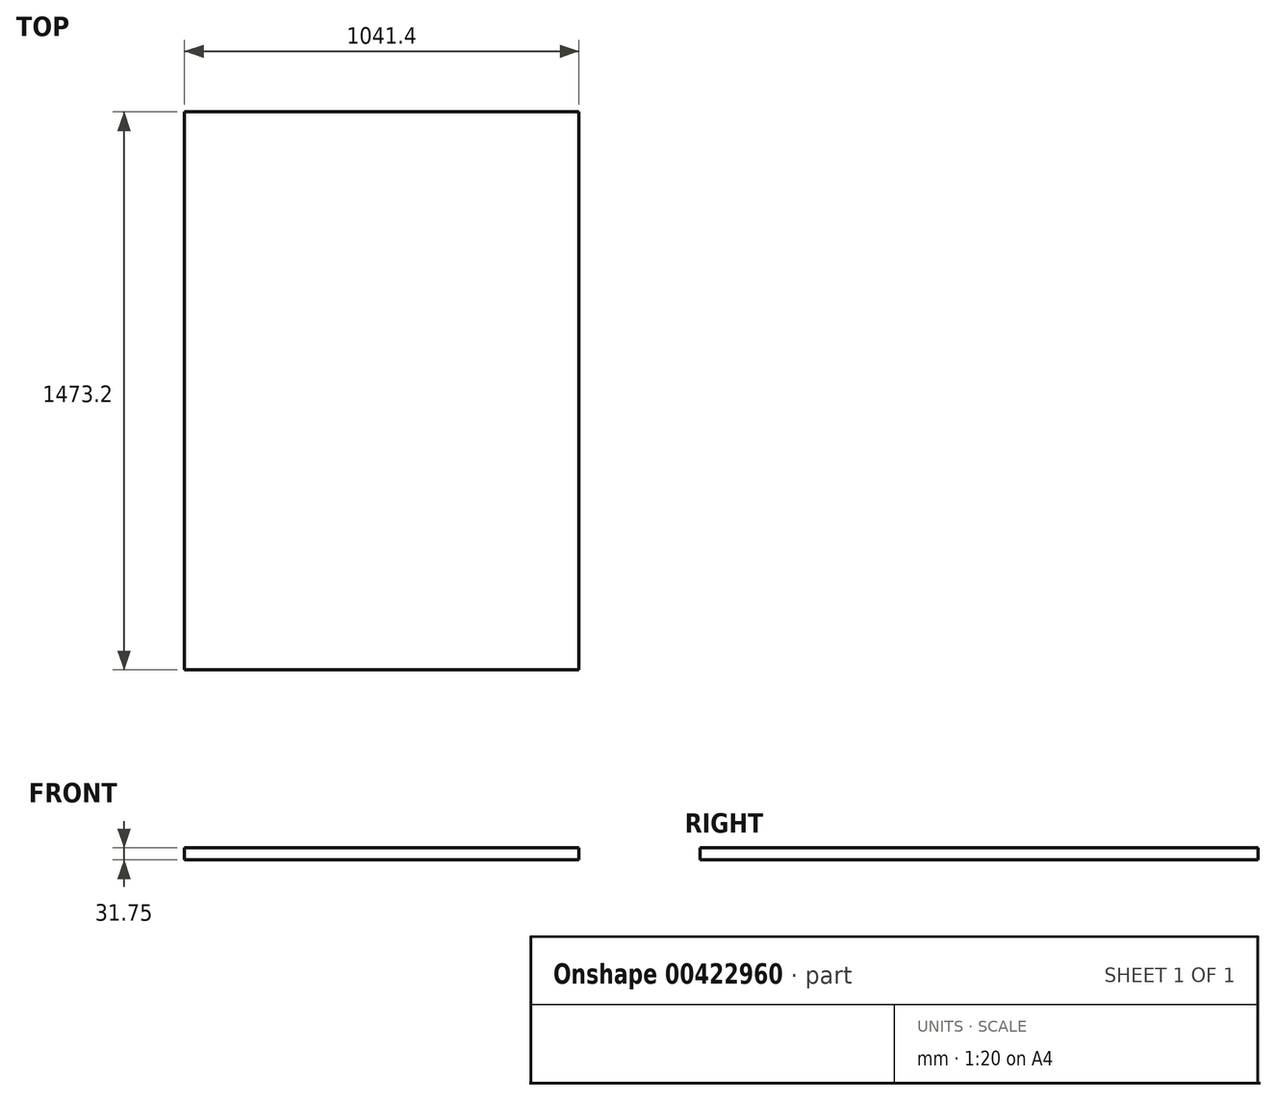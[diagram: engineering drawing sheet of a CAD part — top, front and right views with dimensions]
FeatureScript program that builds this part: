
annotation { "Feature Type Name" : "Feature", "Feature Type Description" : "" }
export const myFeature = defineFeature(function(context is Context, id is Id, definition is map)
    precondition{}
    {
        {
            var Q0;
            Q0=qCreatedBy(makeId("Top.planeOp"),FACE);
            var sketch = newSketch(context, id + "F0", { "sketchPlane" : qUnion([Q0])});
            skLineSegment(sketch, "E0.bottom", {"start": v(520.7, 736.6) * mm, "end": v(-520.7, 736.6) * mm});
            skLineSegment(sketch, "E0.top", {"start": v(520.7, -736.6) * mm, "end": v(-520.7, -736.6) * mm});
            skLineSegment(sketch, "E0.left", {"start": v(520.7, 736.6) * mm, "end": v(520.7, -736.6) * mm});
            skLineSegment(sketch, "E0.right", {"start": v(-520.7, 736.6) * mm, "end": v(-520.7, -736.6) * mm});
            skPoint(sketch, "E0.middle", {"position": v(0, 0) * mm});
            skSolve(sketch);
        }
        {
            var Q0;
            Q0 = qSketchRegion(id + "F0", true);
            extrude(context, id + "F1", {"entities" : qUnion([Q0]), "depth" : 31.75 * mm, "offsetDistance" : 25.4 * mm});
        }
    });
